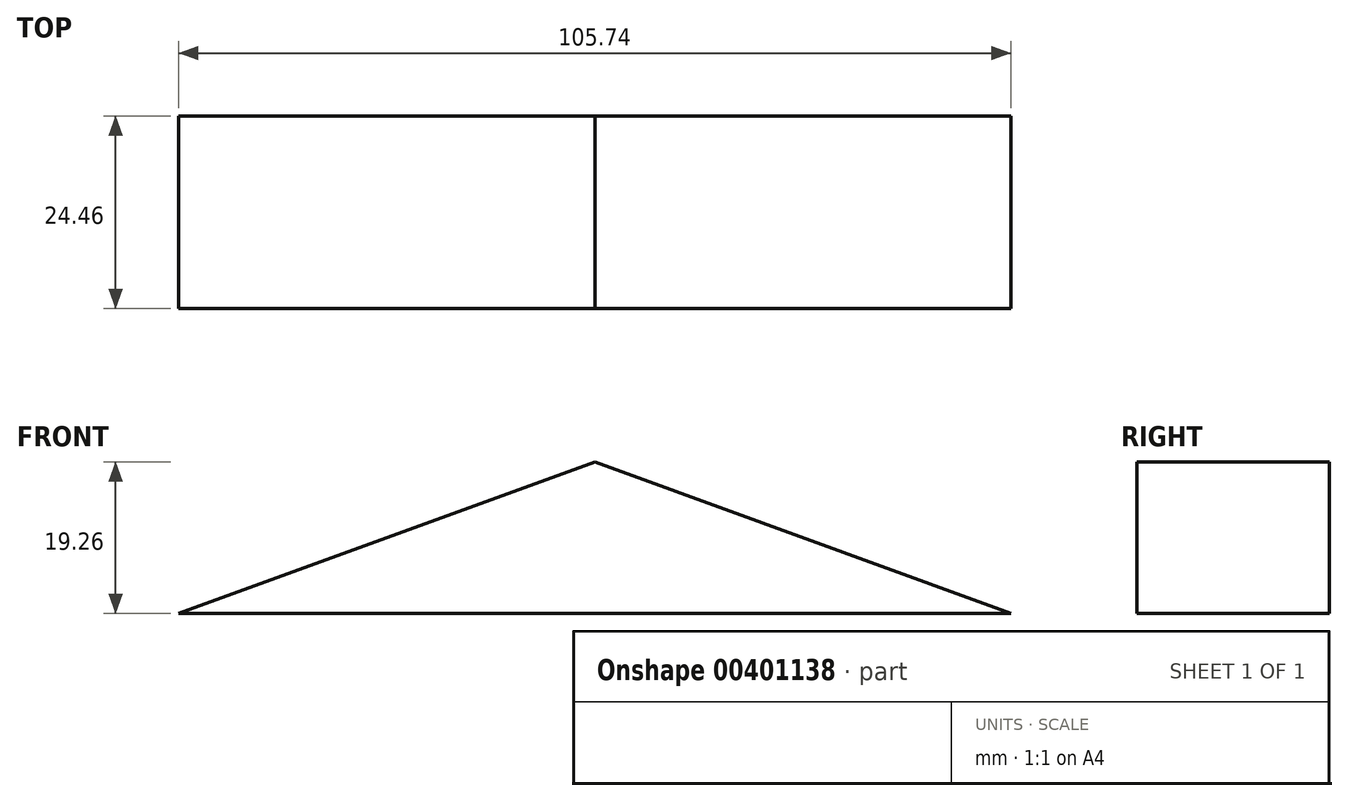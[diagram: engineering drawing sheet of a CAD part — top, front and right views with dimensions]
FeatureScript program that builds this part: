
annotation { "Feature Type Name" : "Feature", "Feature Type Description" : "" }
export const myFeature = defineFeature(function(context is Context, id is Id, definition is map)
    precondition{}
    {
        {
            var Q0;
            Q0=qCreatedBy(makeId("Front.planeOp"),FACE);
            var sketch = newSketch(context, id + "F0", { "sketchPlane" : qUnion([Q0])});
            skLineSegment(sketch, "E0", {"start": v(-74.04, 0) * mm, "end": v(31.7, 0) * mm});
            skLineSegment(sketch, "E1", {"start": v(-21.17, 19.26) * mm, "end": v(-74.04, 0) * mm});
            skLineSegment(sketch, "E2", {"start": v(-21.17, 19.26) * mm, "end": v(31.7, 0) * mm});
            skSolve(sketch);
        }
        {
            var Q0;
            Q0 = qSketchRegion(id + "F0", true);
            extrude(context, id + "F1", {"entities" : qUnion([Q0]), "depth" : 24.46 * mm});
        }
    });
